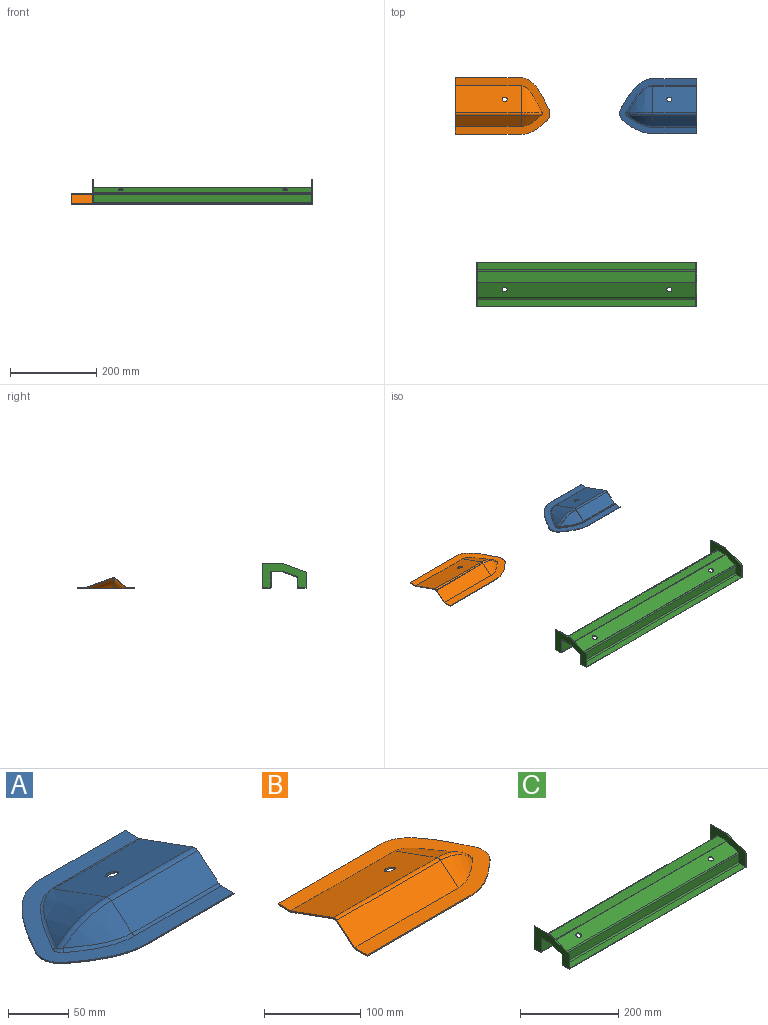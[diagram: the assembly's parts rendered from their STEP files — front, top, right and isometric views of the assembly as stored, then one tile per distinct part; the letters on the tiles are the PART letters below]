
ASSEMBLY  parts=3 mates=2
PART A: 40 faces, bbox 180.8x128.1x48.6 mm
  f0: cone r=66.67mm half-angle=20deg, axis (0,-1,0), area 2603.1mm2, adj f5,f8,f20,f21,f33
  f1: cone r=90.27mm half-angle=40deg, axis (0,1,0), area 1183.5mm2, adj f5,f9,f21
  f2: cone r=66.67mm half-angle=40deg, axis (0,1,0), area 1221.4mm2, adj f4,f10,f25
  f3: cone r=92.08mm half-angle=20deg, axis (0,-1,0), area 2605.5mm2, adj f4,f11,f27
  f4: torus R=85.72mm, axis (0,1,0), area 371.7mm2, adj f2,f3,f12,f26
  f5: torus R=83.92mm, axis (0,-1,0), area 364.7mm2, adj f0,f1,f13,f21
  f6: plane 127.26x24.63mm, normal (1,0,0), area 222.5mm2, adj f7,f8,f9,f10,f11,f12,f13,f14
  f7: plane 177.68x125.68mm, normal (0,0,-1), area 6285.3mm2, adj f6,f8,f29,f30,f31,f32,f33,f34
  f8: plane 101.62x61.81mm, normal (0,-0.34,-0.94), area 6578.5mm2, adj f0,f6,f7,f13,f33,f39
  f9: plane 101.6x25.43mm, normal (0,0.64,-0.77), area 3372.3mm2, adj f1,f6,f13,f22,f29
  f10: plane 101.6x24.49mm, normal (0,-0.64,0.77), area 3248.2mm2, adj f2,f6,f12,f24
  f11: plane 101.6x61.55mm, normal (0,0.34,0.94), area 6552.3mm2, adj f3,f6,f12,f28,f39
  f12: cylinder r=5.59mm len=101.6mm, axis (-1,0,0), area 594.5mm2, adj f4,f6,f10,f11
  f13: cylinder r=5.59mm len=101.6mm, axis (1,0,0), area 594.5mm2, adj f5,f6,f8,f9
  f14: plane 101.6x0.79mm, normal (0,-1,0), area 80.6mm2, adj f6,f15,f19,f34
  f15: bspline ~68.29x29.28mm, area 60.1mm2, adj f14,f16,f19,f35
  f16: bspline ~27.28x8.63mm, area 24.2mm2, adj f15,f17,f19,f36
  f17: bspline ~74.25x70.71mm, area 85.1mm2, adj f16,f18,f19,f37
  f18: plane 101.6x0.79mm, normal (0,1,0), area 80.6mm2, adj f6,f17,f19,f38
  f19: plane 178.51x127.26mm, normal (0,0,1), area 5933.6mm2, adj f6,f14,f15,f16,f17,f18,f24,f25
  f20: bspline ~26.38x16.65mm, area 45.4mm2, adj f0,f21,f23,f32
  f21: plane 58.75x47.35mm, normal (0,0,1), area 29.1mm2, adj f0,f1,f5,f20,f22,f23
  f22: bspline ~57.73x27.14mm, area 138.8mm2, adj f9,f21,f23,f30
  f23: bspline ~5.5x3.15mm, area 10.4mm2, adj f20,f21,f22,f31
  f24: cylinder r=5.08mm len=101.6mm, axis (1,0,0), area 360.3mm2, adj f6,f10,f19,f25
  f25: bspline ~73.86x33.64mm, area 256.7mm2, adj f2,f19,f24,f26
  f26: bspline ~12.55x7.56mm, area 36.7mm2, adj f4,f19,f25,f27
  f27: bspline ~73.75x69.04mm, area 255.2mm2, adj f3,f19,f26,f28
  f28: cylinder r=5.08mm len=101.6mm, axis (-1,0,0), area 180.2mm2, adj f6,f11,f19,f27
  f29: cylinder r=0.79mm len=101.6mm, axis (-1,0,0), area 56.3mm2, adj f6,f7,f9,f30
  f30: bspline ~73.86x28.16mm, area 35.7mm2, adj f7,f22,f29,f31
  f31: bspline ~7.01x3.49mm, area 3.5mm2, adj f7,f23,f30,f32
  f32: bspline ~22x12.97mm, area 11.6mm2, adj f7,f20,f31,f33
  f33: bspline ~58.55x46.25mm, area 28.5mm2, adj f0,f7,f8,f32
  f34: cylinder r=0.79mm len=101.6mm, axis (-1,0,0), area 126.7mm2, adj f6,f7,f14,f35
  f35: bspline ~78.53x31.22mm, area 94.2mm2, adj f7,f15,f34,f36
  f36: bspline ~30.56x10.81mm, area 37.4mm2, adj f7,f16,f35,f37
  f37: bspline ~80.55x78.65mm, area 133.3mm2, adj f7,f17,f36,f38
  f38: cylinder r=0.79mm len=101.6mm, axis (1,0,0), area 126.7mm2, adj f6,f7,f18,f37
  f39: cylinder r=5.71mm len=11.43mm, axis (0,0.34,0.94), area 57mm2, adj f8,f11
PART B: 21 faces, bbox 221.6x133.4x46.4 mm
  f0: cone r=63.5mm half-angle=40deg, axis (0,1,0), area 1116.9mm2, adj f5,f11,f19
  f1: cone r=38.1mm half-angle=40deg, axis (0,1,0), area 1073.2mm2, adj f6,f7,f13
  f2: cone r=61.69mm half-angle=20deg, axis (0,-1,0), area 2146.6mm2, adj f6,f8,f13
  f3: cone r=38.1mm half-angle=20deg, axis (0,-1,0), area 2239.4mm2, adj f9,f11,f19
  f4: plane 131.05x24.7mm, normal (-1,0,0), area 228.4mm2, adj f5,f6,f7,f8,f9,f10,f12,f14
  f5: plane 152.4x26.13mm, normal (0,-0.64,0.77), area 5198.8mm2, adj f0,f4,f10,f19
  f6: plane 221.51x133.42mm, normal (0,0,-1), area 9049.4mm2, adj f1,f2,f4,f7,f8,f13,f14,f15
  f7: plane 152.4x25.87mm, normal (0,0.64,-0.77), area 5147.2mm2, adj f1,f4,f6,f12
  f8: plane 152.4x62.07mm, normal (0,-0.34,-0.94), area 9963.9mm2, adj f2,f4,f6,f12,f20
  f9: plane 152.4x62.67mm, normal (0,0.34,0.94), area 10061mm2, adj f3,f4,f10,f19,f20
  f10: cylinder r=5.08mm len=152.4mm, axis (1,0,0), area 810.7mm2, adj f4,f5,f9,f11
  f11: torus R=57.72mm, axis (0,-1,0), area 293.5mm2, adj f0,f3,f10,f19
  f12: cylinder r=5.08mm len=152.4mm, axis (-1,0,0), area 810.7mm2, adj f4,f7,f8,f13
  f13: torus R=55.92mm, axis (0,1,0), area 288.1mm2, adj f1,f2,f6,f12
  f14: plane 152.4x1.59mm, normal (0,1,0), area 241.9mm2, adj f4,f6,f15,f19
  f15: bspline ~73.05x64.5mm, area 162.4mm2, adj f6,f14,f16,f19
  f16: bspline ~27.1x7.85mm, area 47mm2, adj f6,f15,f17,f19
  f17: bspline ~58.99x30.89mm, area 108.2mm2, adj f6,f16,f18,f19
  f18: plane 152.4x1.59mm, normal (0,-1,0), area 241.9mm2, adj f4,f6,f17,f19
  f19: plane 219.14x131.05mm, normal (0,0,1), area 8825.6mm2, adj f0,f3,f4,f5,f9,f11,f14,f15
  f20: cylinder r=5.71mm len=11.43mm, axis (0,0.34,0.94), area 57mm2, adj f8,f9
PART C: 40 faces, bbox 509.6x101.9x57.2 mm
  f0: plane 34.15x14.45mm, normal (-1,0,0), area 5.9mm2, adj f9,f10,f11,f20,f31,f32
  f1: plane 506.41x32.28mm, normal (0,-0.34,0.94), area 17189.7mm2, adj f16,f19,f28,f37,f38,f39
  f2: plane 506.41x20mm, normal (0,-1,0), area 10129.2mm2, adj f16,f19,f28,f29
  f3: plane 506.41x15.88mm, normal (0,0,1), area 8039.3mm2, adj f7,f16,f19,f29
  f4: plane 506.41x15.88mm, normal (0,0,1), area 8039.3mm2, adj f14,f16,f19,f35
  f5: plane 506.41x31.75mm, normal (0,1,0), area 16078.6mm2, adj f16,f19,f35,f36
  f6: plane 506.41x24.87mm, normal (0,0,1), area 12595.6mm2, adj f16,f19,f36,f37
  f7: plane 508x35.19mm, normal (0,-1,0), area 859.8mm2, adj f3,f8,f15,f16,f19,f27
  f8: plane 509.59x17.46mm, normal (0,0,-1), area 8898.7mm2, adj f7,f15,f21,f24,f30
  f9: plane 509.59x22.7mm, normal (0,1,0), area 10438.7mm2, adj f0,f15,f20,f24,f30,f31
  f10: plane 508x30.97mm, normal (0,0.34,-0.94), area 16537.4mm2, adj f0,f15,f31,f32,f38,f39
  f11: plane 509.59x24.38mm, normal (0,0,-1), area 11725.1mm2, adj f0,f15,f20,f24,f32,f33
  f12: plane 509.59x31.75mm, normal (0,-1,0), area 16179.4mm2, adj f15,f24,f33,f34
  f13: plane 509.59x17.46mm, normal (0,0,-1), area 8898.7mm2, adj f14,f15,f24,f34
  f14: plane 509.59x57.15mm, normal (0,1,0), area 980.3mm2, adj f4,f13,f15,f16,f19,f23,f24,f25
  f15: plane 101.6x57.15mm, normal (1,0,0), area 3173.9mm2, adj f7,f8,f9,f10,f11,f12,f13,f14
  f16: plane 101.6x55.56mm, normal (-1,0,0), area 2908mm2, adj f1,f2,f3,f4,f5,f6,f7,f14
  f17: plane 51.61x18.78mm, normal (0,-0.34,0.94), area 87.2mm2, adj f15,f16,f26,f27
  f18: plane 43.64x1.59mm, normal (0,0,1), area 69.3mm2, adj f15,f16,f25,f26
  f19: plane 101.89x57.15mm, normal (1,0,0), area 2919.4mm2, adj f1,f2,f3,f4,f5,f6,f7,f14
  f20: plane 32.77x12.22mm, normal (0,0.35,-0.94), area 55.5mm2, adj f0,f9,f11,f24
  f21: plane 37.12x1.59mm, normal (0,-1,-0.01), area 58.9mm2, adj f8,f19,f22,f24
  f22: plane 53.69x20.03mm, normal (0,-0.35,0.94), area 91mm2, adj f19,f21,f23,f24
  f23: plane 48.19x1.59mm, normal (0,0,1), area 76.5mm2, adj f14,f19,f22,f24
  f24: plane 101.89x57.15mm, normal (-1,0,0), area 3179.5mm2, adj f8,f9,f11,f12,f13,f14,f20,f21
  f25: cylinder r=3.17mm len=3.18mm, axis (1,0,0), area 7.9mm2, adj f14,f15,f16,f18
  f26: cylinder r=3.17mm len=1.59mm, axis (1,0,0), area 1.8mm2, adj f15,f16,f17,f18
  f27: cylinder r=3.17mm len=2.98mm, axis (-1,0,0), area 6.2mm2, adj f7,f15,f16,f17
  f28: cylinder r=3.17mm len=506.41mm, axis (1,0,0), area 1964.4mm2, adj f1,f2,f16,f19
  f29: cylinder r=3.17mm len=506.41mm, axis (1,0,0), area 2525.6mm2, adj f2,f3,f16,f19
  f30: cylinder r=3.17mm len=509.59mm, axis (-1,0,0), area 2541.5mm2, adj f8,f9,f15,f24
  f31: cylinder r=3.17mm len=508mm, axis (1,0,0), area 1970.5mm2, adj f0,f9,f10,f15
  f32: cylinder r=3.17mm len=508mm, axis (1,0,0), area 563mm2, adj f0,f10,f11,f15
  f33: cylinder r=3.17mm len=509.59mm, axis (1,0,0), area 2541.5mm2, adj f11,f12,f15,f24
  f34: cylinder r=3.17mm len=509.59mm, axis (-1,0,0), area 2541.5mm2, adj f12,f13,f15,f24
  f35: cylinder r=3.17mm len=506.41mm, axis (1,0,0), area 2525.6mm2, adj f4,f5,f16,f19
  f36: cylinder r=3.17mm len=506.41mm, axis (-1,0,0), area 2525.6mm2, adj f5,f6,f16,f19
  f37: cylinder r=3.17mm len=506.41mm, axis (-1,0,0), area 561.2mm2, adj f1,f6,f16,f19
  f38: cylinder r=5.71mm len=11.43mm, axis (0,-0.34,0.94), area 57mm2, adj f1,f10
  f39: cylinder r=5.71mm len=11.43mm, axis (0,-0.34,0.94), area 57mm2, adj f1,f10
PLACE A at identity
PLACE B at identity
PLACE C at identity
MATE fastened A.f7 <-> B.f6  axis (0,0,1) through (0,0,0)mm
MATE fastened C.f8 <-> B.f6  axis (0,0,1) through (0,0,0)mm
